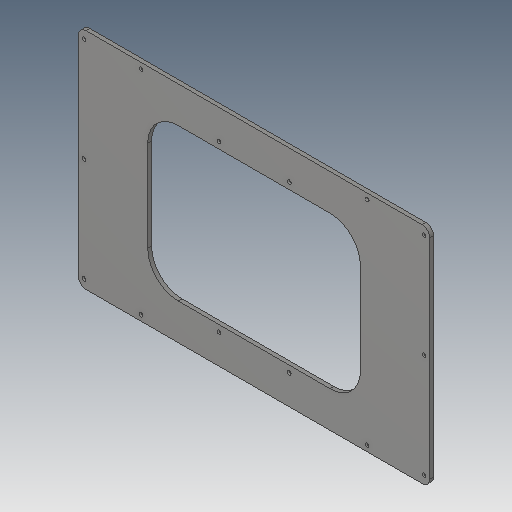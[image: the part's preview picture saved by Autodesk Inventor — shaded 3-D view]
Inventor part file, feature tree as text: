
AUTODESK INVENTOR PART (.ipt)
format: ipt  version: 2023.5 (Build 275446000, 446)  size: 122,368 bytes
history: native  units: in
note: dims shown in document units (in); Inventor stores cm internally (conversion verified against a paired STEP export)
features: fillet x1
ambient origin geometry x8: Origin, YZ Plane, XZ Plane, XY Plane, X Axis, Y Axis, Z Axis, Center Point
bodies: Solid1 (feature_tree)
feature tree (1):
  fillet  "Fillet2"  [1 undecoded]
note: 1 required parameter value undecoded (feature->parameter linkage not recoverable at this tier; creation-order binding heuristic only, values carry confidence <= 0.55)
